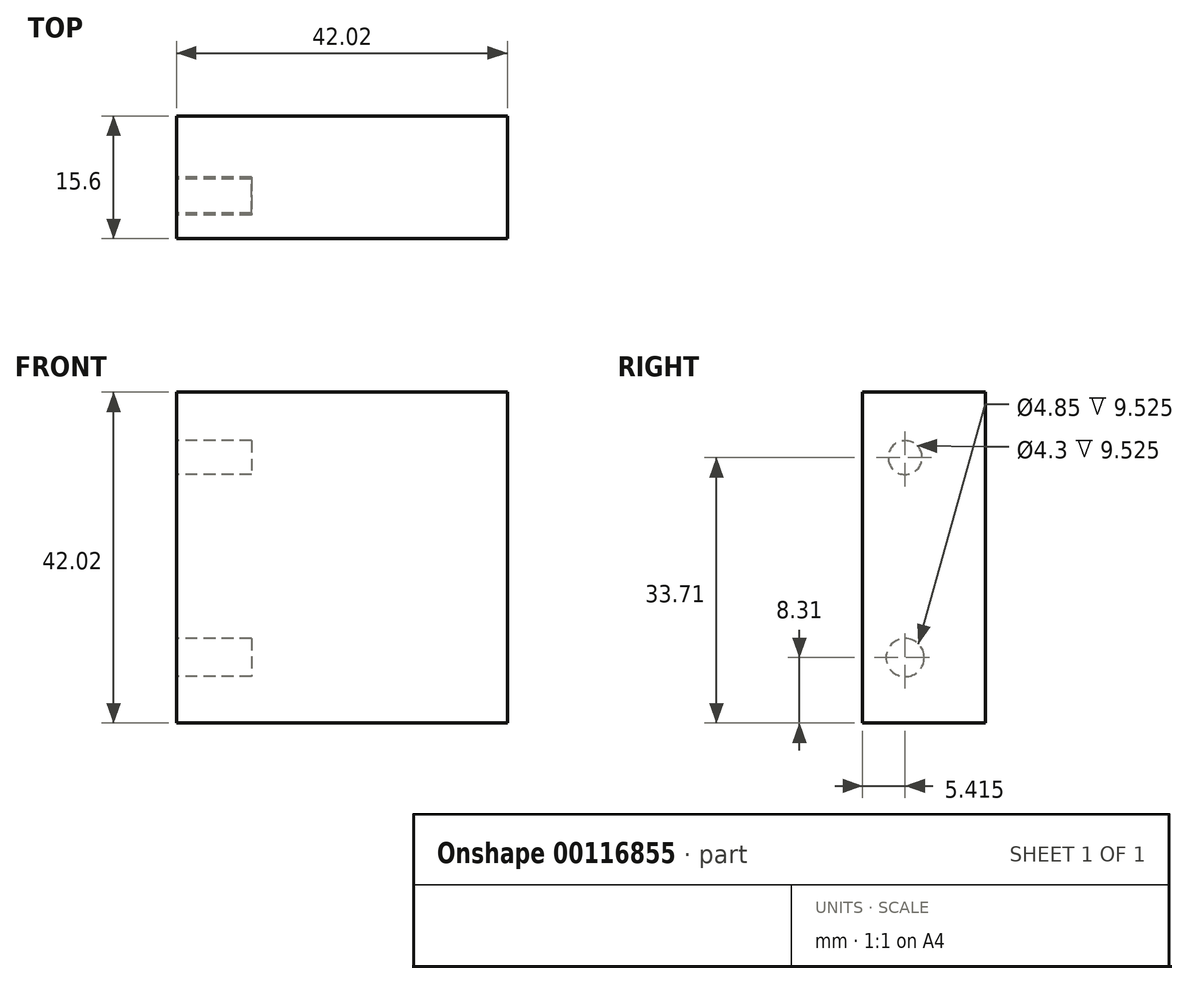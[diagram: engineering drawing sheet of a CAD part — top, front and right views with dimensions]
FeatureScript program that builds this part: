
annotation { "Feature Type Name" : "Feature", "Feature Type Description" : "" }
export const myFeature = defineFeature(function(context is Context, id is Id, definition is map)
    precondition{}
    {
        {
            var Q0;
            Q0=qCreatedBy(makeId("Front.planeOp"),FACE);
            var sketch = newSketch(context, id + "F0", { "sketchPlane" : qUnion([Q0])});
            skLineSegment(sketch, "E0.bottom", {"start": v(21, 21) * mm, "end": v(-21, 21) * mm});
            skLineSegment(sketch, "E0.top", {"start": v(21, -21) * mm, "end": v(-21, -21) * mm});
            skLineSegment(sketch, "E0.left", {"start": v(21, 21) * mm, "end": v(21, -21) * mm});
            skLineSegment(sketch, "E0.right", {"start": v(-21, 21) * mm, "end": v(-21, -21) * mm});
            skPoint(sketch, "E0.middle", {"position": v(0, 0) * mm});
            skSolve(sketch);
        }
        {
            var Q0;
            Q0=makeQuery(id+"F0.imprint","IMPRINT",FACE,{"disambiguationData":[TD([[makeQuery(id+"F0.imprint","IMPRINT",EDGE,{"derivedFrom":sQuery(id+"F0.wireOp",EDGE,"E0.bottom")}),1.0]])]});
            extrude(context, id + "F1", {"entities" : qUnion([Q0]), "depth" : 15.6 * mm});
        }
        {
            var Q0;
            Q0=makeQuery(id+"F1.opExtrude","SWEPT_FACE",FACE,{"disambiguationData":[OSD([sQuery(id+"F0.wireOp",EDGE,"E0.right")])]});
            var sketch = newSketch(context, id + "F2", { "sketchPlane" : qUnion([Q0])});
            skCircle(sketch, "E1", {"center": v(10.19, 12.7) * mm, "radius": 2.15 * mm});
            skCircle(sketch, "E2", {"center": v(10.19, -12.7) * mm, "radius": 2.43 * mm});
            skSolve(sketch);
        }
        {
            var Q0;
            Q0=makeQuery(id+"F2.imprint","IMPRINT",FACE,{"disambiguationData":[TD([[makeQuery(id+"F2.imprint","IMPRINT",EDGE,{"derivedFrom":sQuery(id+"F2.wireOp",EDGE,"E1")}),1.0]])]});
            var Q1;
            Q1=makeQuery(id+"F2.imprint","IMPRINT",FACE,{"disambiguationData":[TD([[makeQuery(id+"F2.imprint","IMPRINT",EDGE,{"derivedFrom":sQuery(id+"F2.wireOp",EDGE,"E2")}),1.0]])]});
            extrude(context, id + "F3", {"entities" : qUnion([Q0, Q1]), "operationType" : NewBodyOperationType.REMOVE, "oppositeDirection" : true, "depth" : 9.52 * mm});
        }
    });
